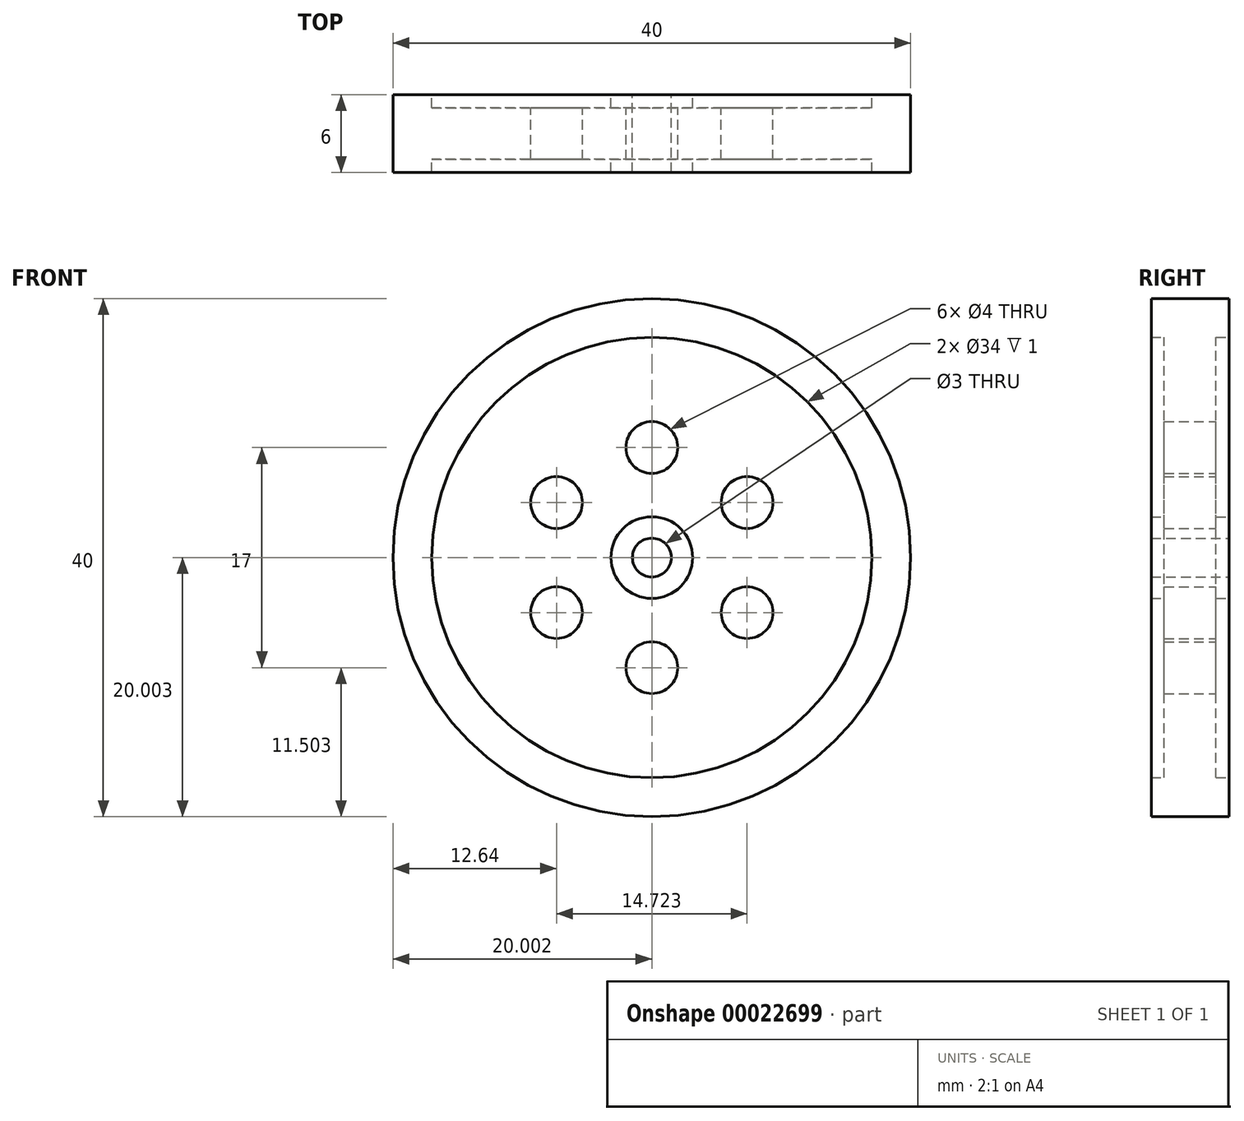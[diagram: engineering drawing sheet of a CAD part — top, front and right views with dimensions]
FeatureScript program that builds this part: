
annotation { "Feature Type Name" : "Feature", "Feature Type Description" : "" }
export const myFeature = defineFeature(function(context is Context, id is Id, definition is map)
    precondition{}
    {
        {
            var Q0;
            Q0=qCreatedBy(makeId("Front.planeOp"),FACE);
            var sketch = newSketch(context, id + "F0", { "sketchPlane" : qUnion([Q0])});
            skCircle(sketch, "E0", {"center": v(27.63, 24.44) * mm, "radius": 20 * mm});
            skCircle(sketch, "E1", {"center": v(27.63, 24.44) * mm, "radius": 17 * mm});
            skCircle(sketch, "E2", {"center": v(27.63, 24.44) * mm, "radius": 3.15 * mm});
            skCircle(sketch, "E3", {"center": v(27.63, 24.44) * mm, "radius": 1.5 * mm});
            skLineSegment(sketch, "E4", {"start": v(27.63, 24.44) * mm, "end": v(27.63, 7.44) * mm});
            skCircle(sketch, "E5", {"center": v(27.63, 15.94) * mm, "radius": 2 * mm});
            skCircle(sketch, "E6.1.0", {"center": v(35, 20.2) * mm, "radius": 2 * mm});
            skCircle(sketch, "E6.2.0", {"center": v(35, 28.7) * mm, "radius": 2 * mm});
            skCircle(sketch, "E6.3.0", {"center": v(27.63, 32.94) * mm, "radius": 2 * mm});
            skCircle(sketch, "E6.4.0", {"center": v(20.27, 28.7) * mm, "radius": 2 * mm});
            skCircle(sketch, "E6.5.0", {"center": v(20.27, 20.2) * mm, "radius": 2 * mm});
            skSolve(sketch);
        }
        {
            var Q0;
            Q0=makeQuery(id+"F0.imprint","IMPRINT",FACE,{"disambiguationData":[TD([[makeQuery(id+"F0.imprint","IMPRINT",EDGE,{"derivedFrom":sQuery(id+"F0.wireOp",EDGE,"E0")}),1.0]])]});
            extrude(context, id + "F1", {"entities" : qUnion([Q0]), "endBound" : BoundingType.SYMMETRIC, "depth" : 6 * mm});
        }
        {
            var Q0;
            Q0=makeQuery(id+"F0.imprint","IMPRINT",FACE,{"disambiguationData":[TD([[makeQuery(id+"F0.imprint","IMPRINT",EDGE,{"derivedFrom":sQuery(id+"F0.wireOp",EDGE,"E1")}),1.0]])]});
            extrude(context, id + "F2", {"entities" : qUnion([Q0]), "operationType" : NewBodyOperationType.ADD, "endBound" : BoundingType.SYMMETRIC, "depth" : 4 * mm});
        }
        {
            var Q0;
            Q0=makeQuery(id+"F0.imprint","IMPRINT",FACE,{"disambiguationData":[TD([[makeQuery(id+"F0.imprint","IMPRINT",EDGE,{"derivedFrom":sQuery(id+"F0.wireOp",EDGE,"E2")}),1.0]])]});
            extrude(context, id + "F3", {"entities" : qUnion([Q0]), "operationType" : NewBodyOperationType.ADD, "endBound" : BoundingType.SYMMETRIC, "depth" : 6 * mm});
        }
    });
